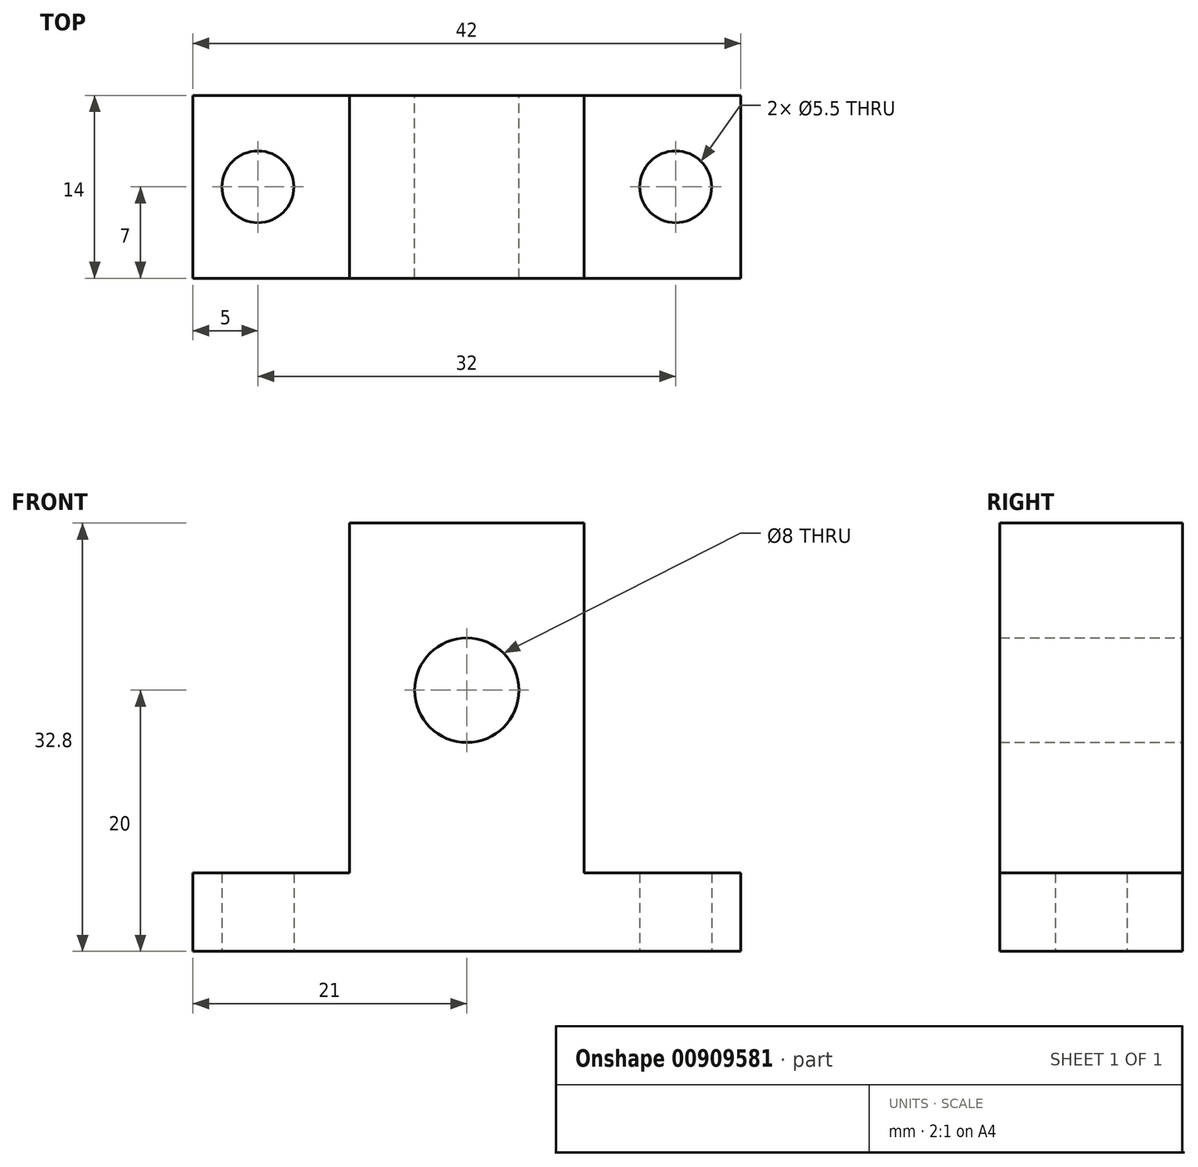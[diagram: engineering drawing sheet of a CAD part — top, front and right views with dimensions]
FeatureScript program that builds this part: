
annotation { "Feature Type Name" : "Feature", "Feature Type Description" : "" }
export const myFeature = defineFeature(function(context is Context, id is Id, definition is map)
    precondition{}
    {
        {
            var Q0;
            Q0=qCreatedBy(makeId("Front.planeOp"),FACE);
            var sketch = newSketch(context, id + "F0", { "sketchPlane" : qUnion([Q0])});
            skLineSegment(sketch, "E0.bottom", {"start": v(9, 13.4) * mm, "end": v(-9, 13.4) * mm});
            skLineSegment(sketch, "E0.top", {"start": v(9, -13.4) * mm, "end": v(-9, -13.4) * mm});
            skLineSegment(sketch, "E0.left", {"start": v(9, 13.4) * mm, "end": v(9, -13.4) * mm});
            skLineSegment(sketch, "E0.right", {"start": v(-9, 13.4) * mm, "end": v(-9, -13.4) * mm});
            skPoint(sketch, "E0.middle", {"position": v(0, 0) * mm});
            skLineSegment(sketch, "E1.bottom", {"start": v(-21, -13.4) * mm, "end": v(21, -13.4) * mm});
            skLineSegment(sketch, "E1.top", {"start": v(-21, -19.4) * mm, "end": v(21, -19.4) * mm});
            skLineSegment(sketch, "E1.left", {"start": v(-21, -13.4) * mm, "end": v(-21, -19.4) * mm});
            skLineSegment(sketch, "E1.right", {"start": v(21, -13.4) * mm, "end": v(21, -19.4) * mm});
            skPoint(sketch, "E2", {"position": v(0, -13.4) * mm});
            skCircle(sketch, "E3", {"center": v(0, 0.6) * mm, "radius": 4 * mm});
            skSolve(sketch);
        }
        {
            var Q0;
            Q0=makeQuery(id+"F0.imprint","IMPRINT",FACE,{"disambiguationData":[TD([[makeQuery(id+"F0.imprint","IMPRINT",EDGE,{"derivedFrom":sQuery(id+"F0.wireOp",EDGE,"E0.bottom")}),1.0]])]});
            var Q1;
            Q1=makeQuery(id+"F0.imprint","IMPRINT",FACE,{"disambiguationData":[TD([[makeQuery(id+"F0.imprint","IMPRINT",EDGE,{"derivedFrom":sQuery(id+"F0.wireOp",EDGE,"E1.top")}),1.0]])]});
            extrude(context, id + "F1", {"entities" : qUnion([Q0, Q1]), "depth" : 14 * mm, "offsetDistance" : 25.4 * mm});
        }
        {
            var Q0;
            Q0=makeQuery(id+"F1.opExtrude","SWEPT_FACE",FACE,{"disambiguationData":[OSD([sQuery(id+"F0.wireOp",EDGE,"E1.top")])]});
            var sketch = newSketch(context, id + "F2", { "sketchPlane" : qUnion([Q0])});
            skLineSegment(sketch, "E4", {"start": v(0, 0) * mm, "end": v(0, 14) * mm, "construction": true});
            skCircle(sketch, "E5", {"center": v(-16, 7) * mm, "radius": 1.59 * mm, "construction": true});
            skPoint(sketch, "E5.centerSnap0", {"position": v(0, 7) * mm});
            skCircle(sketch, "E6.MirrorC", {"center": v(16, 7) * mm, "radius": 1.59 * mm, "construction": true});
            skSolve(sketch);
        }
        {
            var Q0;
            Q0=sQuery(id+"F2.wireOp",VERTEX,"E5.center");
            var Q1;
            Q1=sQuery(id+"F2.wireOp",VERTEX,"E6.MirrorC.center");
            var Q2;
            Q2=makeQuery(id+"F1.opExtrude","SWEPT_BODY",BODY,{"disambiguationData":[OSD([sQuery(id+"F0.wireOp",EDGE,"E0.bottom"),sQuery(id+"F0.wireOp",EDGE,"E0.left"),sQuery(id+"F0.wireOp",EDGE,"E0.right"),sQuery(id+"F0.wireOp",EDGE,"E1.bottom"),sQuery(id+"F0.wireOp",EDGE,"E1.top"),sQuery(id+"F0.wireOp",EDGE,"E1.left"),sQuery(id+"F0.wireOp",EDGE,"E1.right"),sQuery(id+"F0.wireOp",EDGE,"E3")])]});
            hole(context, id + "F3", {"style" : HoleStyle.SIMPLE, "endStyle" : HoleEndStyle.BLIND, "standardTappedOrClearance" : lookupTablePath({ "fit" : "Normal", "standard" : "ISO", "size" : "M5", "type" : "Clearance" }), "standardBlindInLast" : lookupTablePath({ "fit" : "Normal", "standard" : "ISO", "size" : "M5", "type" : "Clearance" }), "holeDiameter" : 5.5 * mm, "majorDiameter" : 5 * mm, "holeDepth" : 13.5 * mm, "isTappedThrough" : true, "tappedDepth" : 11.1 * mm, "tapClearance" : 3, "locations" : qUnion([Q0, Q1]), "scope" : qUnion([Q2])});
        }
    });
